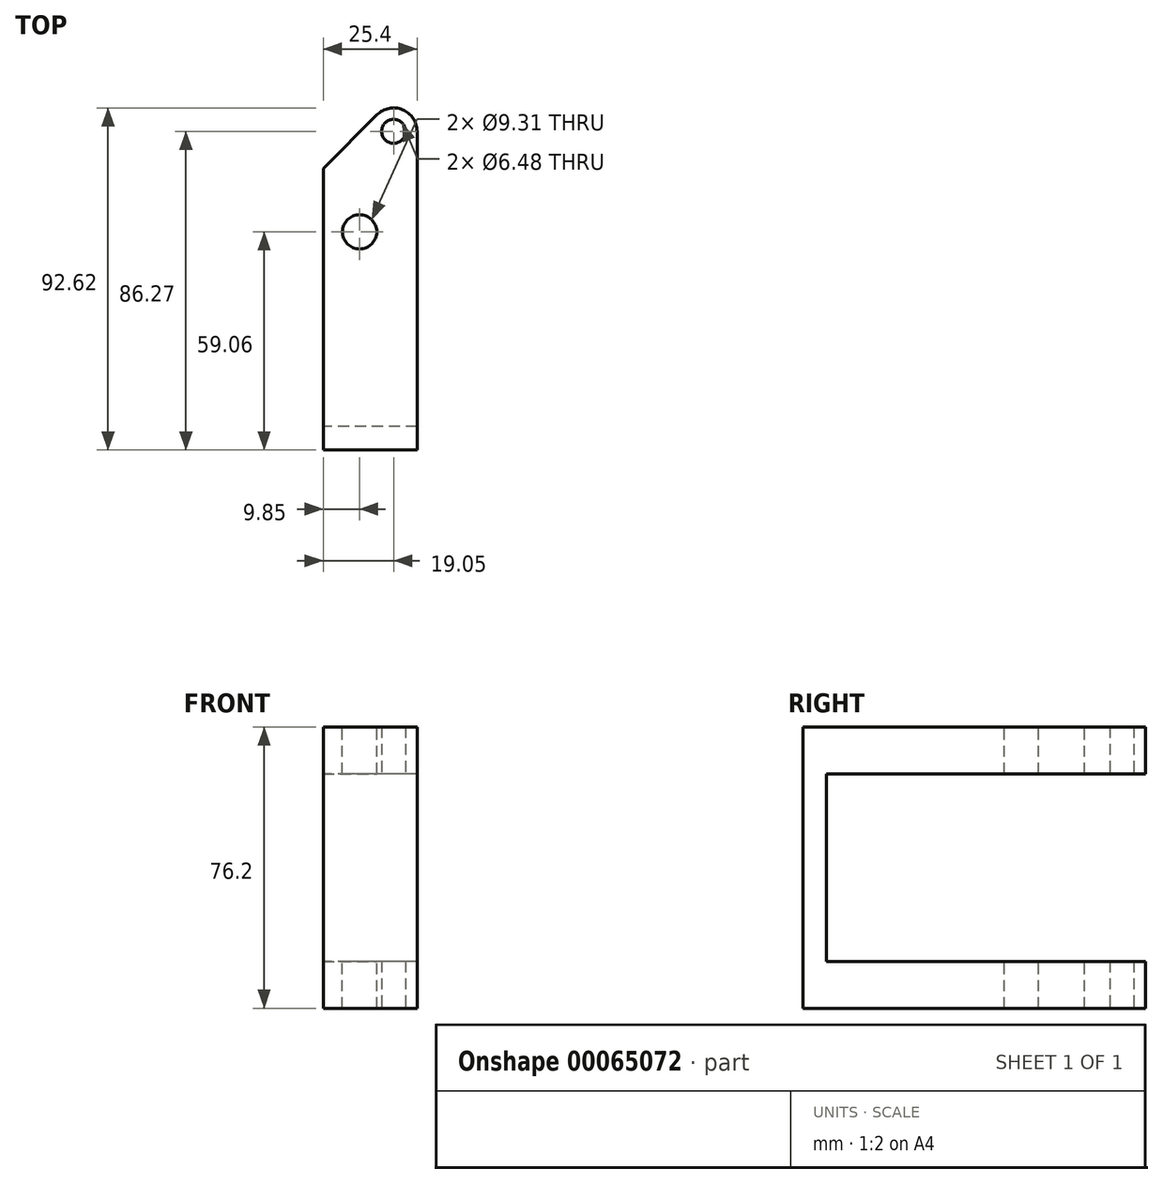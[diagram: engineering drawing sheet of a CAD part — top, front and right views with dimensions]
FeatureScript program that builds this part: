
annotation { "Feature Type Name" : "Feature", "Feature Type Description" : "" }
export const myFeature = defineFeature(function(context is Context, id is Id, definition is map)
    precondition{}
    {
        {
            var Q0;
            Q0=qCreatedBy(makeId("Top.planeOp"),FACE);
            var sketch = newSketch(context, id + "F0", { "sketchPlane" : qUnion([Q0])});
            skLineSegment(sketch, "E0", {"start": v(0, 0) * mm, "end": v(25.4, 0) * mm});
            skLineSegment(sketch, "E1", {"start": v(25.4, 0) * mm, "end": v(25.4, 101.6) * mm});
            skLineSegment(sketch, "E2", {"start": v(25.4, 101.6) * mm, "end": v(0, 76.2) * mm});
            skLineSegment(sketch, "E3", {"start": v(0, 76.2) * mm, "end": v(0, 0) * mm});
            skCircle(sketch, "E4", {"center": v(9.85, 59.06) * mm, "radius": 4.65 * mm});
            skSolve(sketch);
        }
        {
            var Q0;
            Q0=makeQuery(id+"F0.imprint","IMPRINT",FACE,{"disambiguationData":[TD([[makeQuery(id+"F0.imprint","IMPRINT",EDGE,{"derivedFrom":sQuery(id+"F0.wireOp",EDGE,"E0")}),1.0]])]});
            extrude(context, id + "F1", {"entities" : qUnion([Q0]), "oppositeDirection" : true, "depth" : 76.2 * mm});
        }
        {
            var Q0;
            Q0=makeQuery(id+"F1.opExtrude","SWEPT_EDGE",EDGE,{"disambiguationData":[OSD([sQuery(id+"F0.wireOp",EDGE,"E1"),sQuery(id+"F0.wireOp",EDGE,"E2")])]});
            fillet(context, id + "F2", {"entities" : qUnion([Q0]), "radius" : 6.35 * mm, "tangentPropagation" : true, "allowEdgeOverflow" : false});
        }
        {
            var Q0;
            Q0=makeQuery(id+"F1.opExtrude","SWEPT_FACE",FACE,{"disambiguationData":[OSD([sQuery(id+"F0.wireOp",EDGE,"E3")])]});
            var sketch = newSketch(context, id + "F3", { "sketchPlane" : qUnion([Q0])});
            skLineSegment(sketch, "E5.bottom", {"start": v(-6.35, -63.5) * mm, "end": v(-103.46, -63.5) * mm});
            skLineSegment(sketch, "E5.top", {"start": v(-6.35, -12.7) * mm, "end": v(-103.46, -12.7) * mm});
            skLineSegment(sketch, "E5.right", {"start": v(-103.46, -63.5) * mm, "end": v(-103.46, -12.7) * mm});
            skLineSegment(sketch, "E6", {"start": v(-103.46, -38.1) * mm, "end": v(0, -38.1) * mm});
            skLineSegment(sketch, "E7", {"start": v(-6.35, -12.7) * mm, "end": v(-6.35, -63.5) * mm});
            skSolve(sketch);
        }
        {
            var Q0;
            Q0 = qSketchRegion(id + "F3", true);
            extrude(context, id + "F4", {"entities" : qUnion([Q0]), "operationType" : NewBodyOperationType.REMOVE, "endBound" : BoundingType.THROUGH_ALL, "oppositeDirection" : true, "depth" : 25.4 * mm});
        }
        {
            var Q0;
            Q0=makeQuery(id+"F1.opExtrude","CAP_FACE",FACE,{"disambiguationData":[OSD([sQuery(id+"F0.wireOp",EDGE,"E0"),sQuery(id+"F0.wireOp",EDGE,"E1"),sQuery(id+"F0.wireOp",EDGE,"E2"),sQuery(id+"F0.wireOp",EDGE,"E3")])],"isStart":false});
            var sketch = newSketch(context, id + "F5", { "sketchPlane" : qUnion([Q0])});
            skCircle(sketch, "E8", {"center": v(19.05, -86.27) * mm, "radius": 3.24 * mm});
            skSolve(sketch);
        }
        {
            var Q0;
            Q0 = qSketchRegion(id + "F5", true);
            extrude(context, id + "F6", {"entities" : qUnion([Q0]), "operationType" : NewBodyOperationType.REMOVE, "endBound" : BoundingType.THROUGH_ALL, "oppositeDirection" : true, "depth" : 25.4 * mm});
        }
    });
